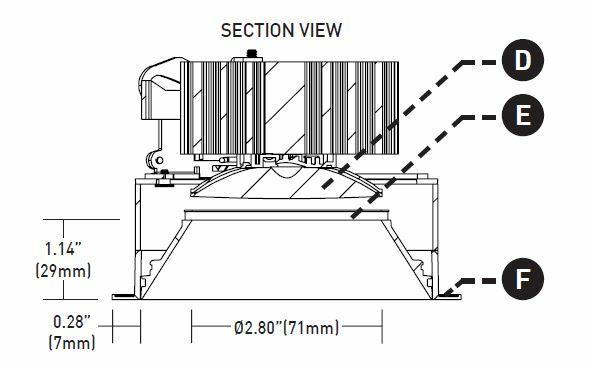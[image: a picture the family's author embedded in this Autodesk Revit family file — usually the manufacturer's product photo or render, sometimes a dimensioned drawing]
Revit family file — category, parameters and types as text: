
# Revit family: Lighting-Pendant-Lucifer-Cylinder-CY2
name_source: partatom
category: Lighting Fixtures
revit_build: Autodesk Revit 2016 (Build: 20170117_1200(x64)
units: mm (PartAtom-declared; Revit-internal decimal feet)

## family parameters
Cut with Voids When Loaded = No
Host = Face
Light Source = Yes
Part Type = Normal
Room Calculation Point = No
Round Connector Dimension = Use Diameter
Shared = No

## types (1)
- CY2
    Apparent Load = 0 VA
    Color Filter = 16777215
    Default Elevation = 48 "
    Description = Surface Cylinder
    Dimming Lamp Color Temperature Shift = <None>
    Emit Shape Visible in Rendering = No
    Emit from Circle Diameter = 3.25 "
    Lamp = LED
    Manufacturer = Lucifer Lighting
    Model = CY2
    Number of Poles = 1
    Photometric Web File = Load File
    Power Factor = 1
    Tilt Angle = -90.00°
    URL = https://www.luciferlighting.com
    Voltage = 0 V

## geometry (parser evidence)
native form markers: Sweep x3
no freeform markers — native parametric forms only
